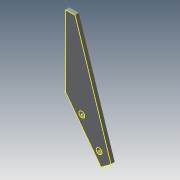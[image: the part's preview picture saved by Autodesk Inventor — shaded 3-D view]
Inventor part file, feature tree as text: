
AUTODESK INVENTOR PART (.ipt)
format: ipt  version: 2013 (Build 170138000, 138)  size: 100,352 bytes
history: native  units: mm
features: sketch x5, extrude x3
ambient origin geometry x8: Origin, YZ Plane, XZ Plane, XY Plane, X Axis, Y Axis, Z Axis, Center Point
bodies: Solid1 (feature_tree)
feature tree (8):
  sketch  "Sketch1"  dims[d4=3.0mm d5=3.0mm d6=2.0mm d7=0.0mm]
  extrude  "Extrusion1"  Depth=2.0mm TaperAngle=0.0deg
  extrude  "Extrusion2"  Depth=2.0mm TaperAngle=0.0deg
  extrude  "Extrusion3"  Depth=2.0mm TaperAngle=0.0deg
  sketch  "Sketch5"
  sketch  "Sketch2"  dims[d8=10.0mm d11=2.0mm d12=0.0mm]
  sketch  "Sketch3"  dims[d13=5.0mm d14=2.0mm d15=0.0mm]
  sketch  "Sketch4"
